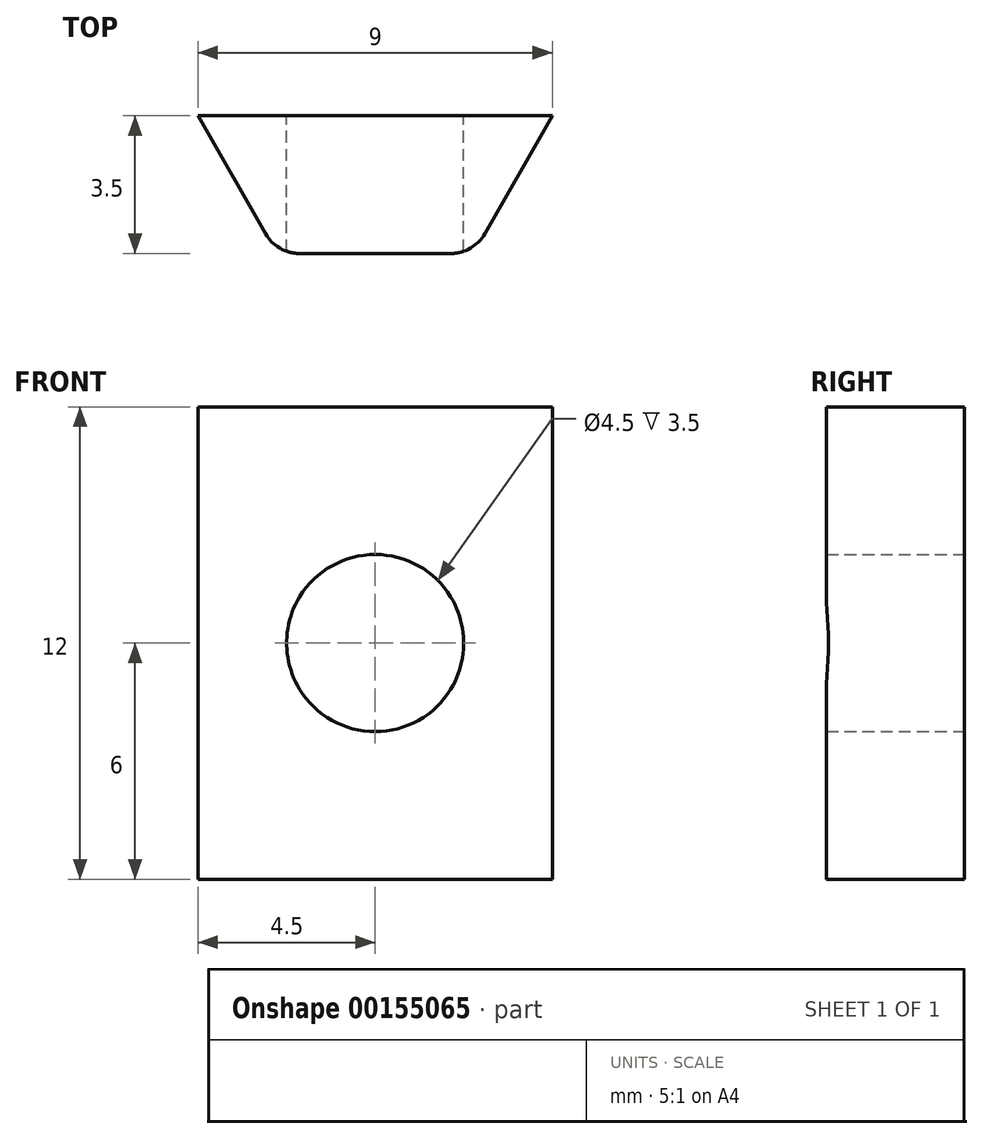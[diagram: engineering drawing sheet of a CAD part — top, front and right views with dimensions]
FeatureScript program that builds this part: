
annotation { "Feature Type Name" : "Feature", "Feature Type Description" : "" }
export const myFeature = defineFeature(function(context is Context, id is Id, definition is map)
    precondition{}
    {
        {
            var Q0;
            Q0=qCreatedBy(makeId("Top.planeOp"),FACE);
            var sketch = newSketch(context, id + "F0", { "sketchPlane" : qUnion([Q0])});
            skLineSegment(sketch, "E0.bottom", {"start": v(4.5, -1.75) * mm, "end": v(-4.5, -1.75) * mm});
            skLineSegment(sketch, "E0.top", {"start": v(4.5, 1.75) * mm, "end": v(-4.5, 1.75) * mm});
            skLineSegment(sketch, "E0.left", {"start": v(4.5, -1.75) * mm, "end": v(4.5, 1.75) * mm});
            skLineSegment(sketch, "E0.right", {"start": v(-4.5, -1.75) * mm, "end": v(-4.5, 1.75) * mm});
            skPoint(sketch, "E0.middle", {"position": v(0, 0) * mm});
            skLineSegment(sketch, "E1", {"start": v(-2.5, -1.75) * mm, "end": v(2.5, -1.75) * mm});
            skLineSegment(sketch, "E2", {"start": v(-4.5, 1.75) * mm, "end": v(-2.5, -1.75) * mm});
            skLineSegment(sketch, "E3", {"start": v(2.5, -1.75) * mm, "end": v(4.5, 1.75) * mm});
            skSolve(sketch);
        }
        {
            var Q0;
            Q0=makeQuery(id+"F0.imprint","IMPRINT",FACE,{"disambiguationData":[TD([[makeQuery(id+"F0.imprint","IMPRINT",EDGE,{"derivedFrom":sQuery(id+"F0.wireOp",EDGE,"E0.top")}),1.0]])]});
            extrude(context, id + "F1", {"entities" : qUnion([Q0]), "depth" : 12 * mm});
        }
        {
            var Q0;
            Q0=makeQuery(id+"F1.opExtrude","SWEPT_FACE",FACE,{"disambiguationData":[OSD([sQuery(id+"F0.wireOp",EDGE,"E0.top")])]});
            var sketch = newSketch(context, id + "F2", { "sketchPlane" : qUnion([Q0])});
            skPoint(sketch, "E4", {"position": v(0, 6) * mm});
            skPoint(sketch, "E4.positionSnap0", {"position": v(4.5, 6) * mm});
            skPoint(sketch, "E4.positionSnap1", {"position": v(0, 0) * mm});
            skSolve(sketch);
        }
        {
            var Q0;
            Q0=sQuery(id+"F2.wireOp",VERTEX,"E4");
            var Q1;
            Q1=makeQuery(id+"F1.opExtrude","SWEPT_BODY",BODY,{"disambiguationData":[OSD([sQuery(id+"F0.wireOp",EDGE,"E0.top"),sQuery(id+"F0.wireOp",EDGE,"E1"),sQuery(id+"F0.wireOp",EDGE,"E2"),sQuery(id+"F0.wireOp",EDGE,"E3")])]});
            hole(context, id + "F3", {"style" : HoleStyle.SIMPLE, "endStyle" : HoleEndStyle.THROUGH, "holeDiameter" : 4.5 * mm, "locations" : qUnion([Q0]), "scope" : qUnion([Q1]), "isTappedThrough" : true});
        }
        {
            var Q0;
            Q0=makeQuery(id+"F1.opExtrude","SWEPT_EDGE",EDGE,{"disambiguationData":[OSD([sQuery(id+"F0.wireOp",EDGE,"E0.bottom"),sQuery(id+"F0.wireOp",EDGE,"E1"),sQuery(id+"F0.wireOp",EDGE,"E3")])]});
            var Q1;
            Q1=makeQuery(id+"F1.opExtrude","SWEPT_EDGE",EDGE,{"disambiguationData":[OSD([sQuery(id+"F0.wireOp",EDGE,"E0.bottom"),sQuery(id+"F0.wireOp",EDGE,"E1"),sQuery(id+"F0.wireOp",EDGE,"E2")])]});
            fillet(context, id + "F4", {"entities" : qUnion([Q0, Q1]), "radius" : 1 * mm, "tangentPropagation" : true, "allowEdgeOverflow" : false});
        }
    });
